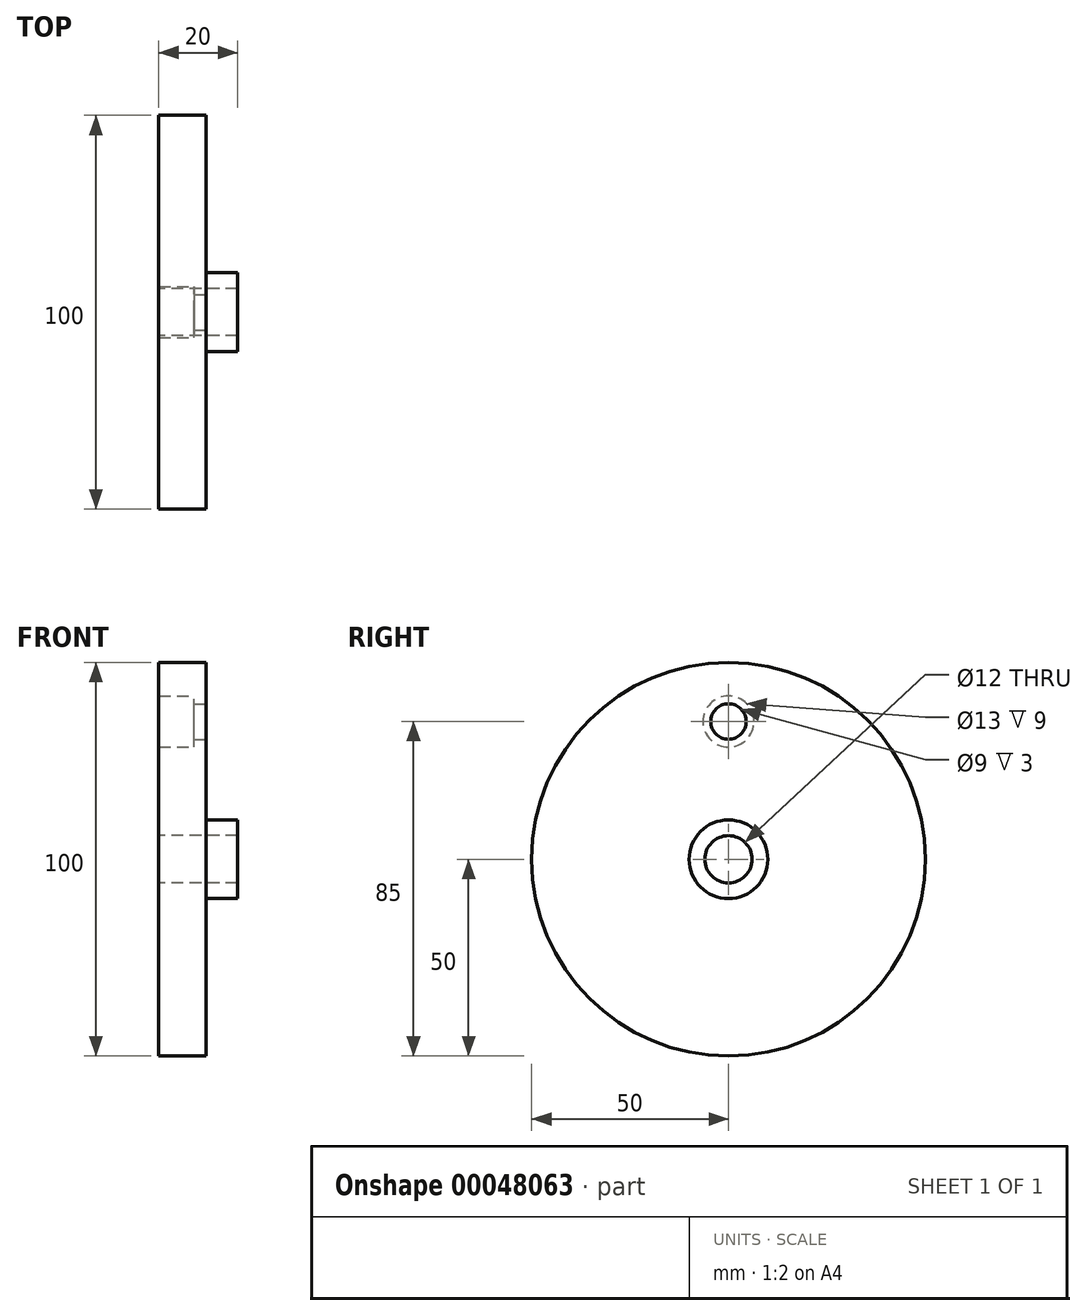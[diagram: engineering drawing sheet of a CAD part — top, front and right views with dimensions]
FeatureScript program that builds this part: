
annotation { "Feature Type Name" : "Feature", "Feature Type Description" : "" }
export const myFeature = defineFeature(function(context is Context, id is Id, definition is map)
    precondition{}
    {
        {
            var Q0;
            Q0=qCreatedBy(makeId("Front.planeOp"),FACE);
            var sketch = newSketch(context, id + "F0", { "sketchPlane" : qUnion([Q0])});
            skLineSegment(sketch, "E0", {"start": v(0, 0) * mm, "end": v(20, 0) * mm});
            skLineSegment(sketch, "E1", {"start": v(20, 0) * mm, "end": v(20, 6) * mm, "construction": true});
            skLineSegment(sketch, "E2", {"start": v(20, 6) * mm, "end": v(0, 6) * mm});
            skLineSegment(sketch, "E3", {"start": v(0, 6) * mm, "end": v(0, 0) * mm, "construction": true});
            skLineSegment(sketch, "E4", {"start": v(20, 6) * mm, "end": v(20, 10) * mm});
            skLineSegment(sketch, "E5", {"start": v(20, 10) * mm, "end": v(12, 10) * mm});
            skLineSegment(sketch, "E6", {"start": v(12, 10) * mm, "end": v(12, 50) * mm});
            skLineSegment(sketch, "E7", {"start": v(12, 50) * mm, "end": v(0, 50) * mm});
            skLineSegment(sketch, "E8", {"start": v(0, 50) * mm, "end": v(0, 6) * mm});
            skLineSegment(sketch, "E9", {"start": v(0, 35) * mm, "end": v(12, 35) * mm});
            skLineSegment(sketch, "E10", {"start": v(0, 35) * mm, "end": v(0, 41.5) * mm});
            skLineSegment(sketch, "E11", {"start": v(0, 41.5) * mm, "end": v(9, 41.5) * mm});
            skLineSegment(sketch, "E12", {"start": v(9, 41.5) * mm, "end": v(9, 39.5) * mm});
            skLineSegment(sketch, "E13", {"start": v(9, 39.5) * mm, "end": v(12, 39.5) * mm});
            skLineSegment(sketch, "E14", {"start": v(12, 39.5) * mm, "end": v(12, 30.5) * mm});
            skLineSegment(sketch, "E15", {"start": v(12, 30.5) * mm, "end": v(9, 30.5) * mm});
            skLineSegment(sketch, "E16", {"start": v(9, 30.5) * mm, "end": v(9, 28.5) * mm});
            skLineSegment(sketch, "E17", {"start": v(9, 28.5) * mm, "end": v(0, 28.5) * mm});
            skLineSegment(sketch, "E18", {"start": v(0, 28.5) * mm, "end": v(0, 41.5) * mm});
            skPoint(sketch, "E19", {"position": v(0, 41.5) * mm});
            skPoint(sketch, "E20", {"position": v(0, 28.5) * mm});
            skPoint(sketch, "E21", {"position": v(12, 30.5) * mm});
            skPoint(sketch, "E22", {"position": v(12, 39.5) * mm});
            skSolve(sketch);
        }
        {
            var Q0;
            {var subQ2=sQuery(id+"F0.wireOp",EDGE,"E7");Q0=makeQuery(id+"F0.imprint","IMPRINT",FACE,{"disambiguationData":[TD([[makeQuery(id+"F0.imprint","IMPRINT",EDGE,{"derivedFrom":subQ2}),1.0]])]});}
            var Q1;
            {var subQ3=sQuery(id+"F0.wireOp",EDGE,"E2");Q1=makeQuery(id+"F0.imprint","IMPRINT",FACE,{"disambiguationData":[TD([[makeQuery(id+"F0.imprint","IMPRINT",EDGE,{"derivedFrom":subQ3}),-1.0]])]});}
            var Q2;
            {var subQ2=sQuery(id+"F0.wireOp",EDGE,"E9");Q2=makeQuery(id+"F0.imprint","IMPRINT",FACE,{"disambiguationData":[TD([[makeQuery(id+"F0.imprint","IMPRINT",EDGE,{"derivedFrom":subQ2}),1.0]])]});}
            var Q3;
            {var subQ1=sQuery(id+"F0.wireOp",EDGE,"E9");Q3=makeQuery(id+"F0.imprint","IMPRINT",FACE,{"disambiguationData":[TD([[makeQuery(id+"F0.imprint","IMPRINT",EDGE,{"derivedFrom":subQ1}),-1.0]])]});}
            var Q4;
            Q4=sQuery(id+"F0.wireOp",EDGE,"E0");
            revolve(context, id + "F1", {"entities" : qUnion([Q0, Q1, Q2, Q3]), "axis" : qUnion([Q4]), "revolveType" : RevolveType.FULL});
        }
        {
            var Q0;
            {var subQ2=sQuery(id+"F0.wireOp",EDGE,"E9");Q0=makeQuery(id+"F0.imprint","IMPRINT",FACE,{"disambiguationData":[TD([[makeQuery(id+"F0.imprint","IMPRINT",EDGE,{"derivedFrom":subQ2}),1.0]])]});}
            var Q1;
            Q1=sQuery(id+"F0.wireOp",EDGE,"E9");
            revolve(context, id + "F2", {"operationType" : NewBodyOperationType.REMOVE, "entities" : qUnion([Q0]), "axis" : qUnion([Q1]), "revolveType" : RevolveType.FULL, "oppositeDirection" : true});
        }
    });
